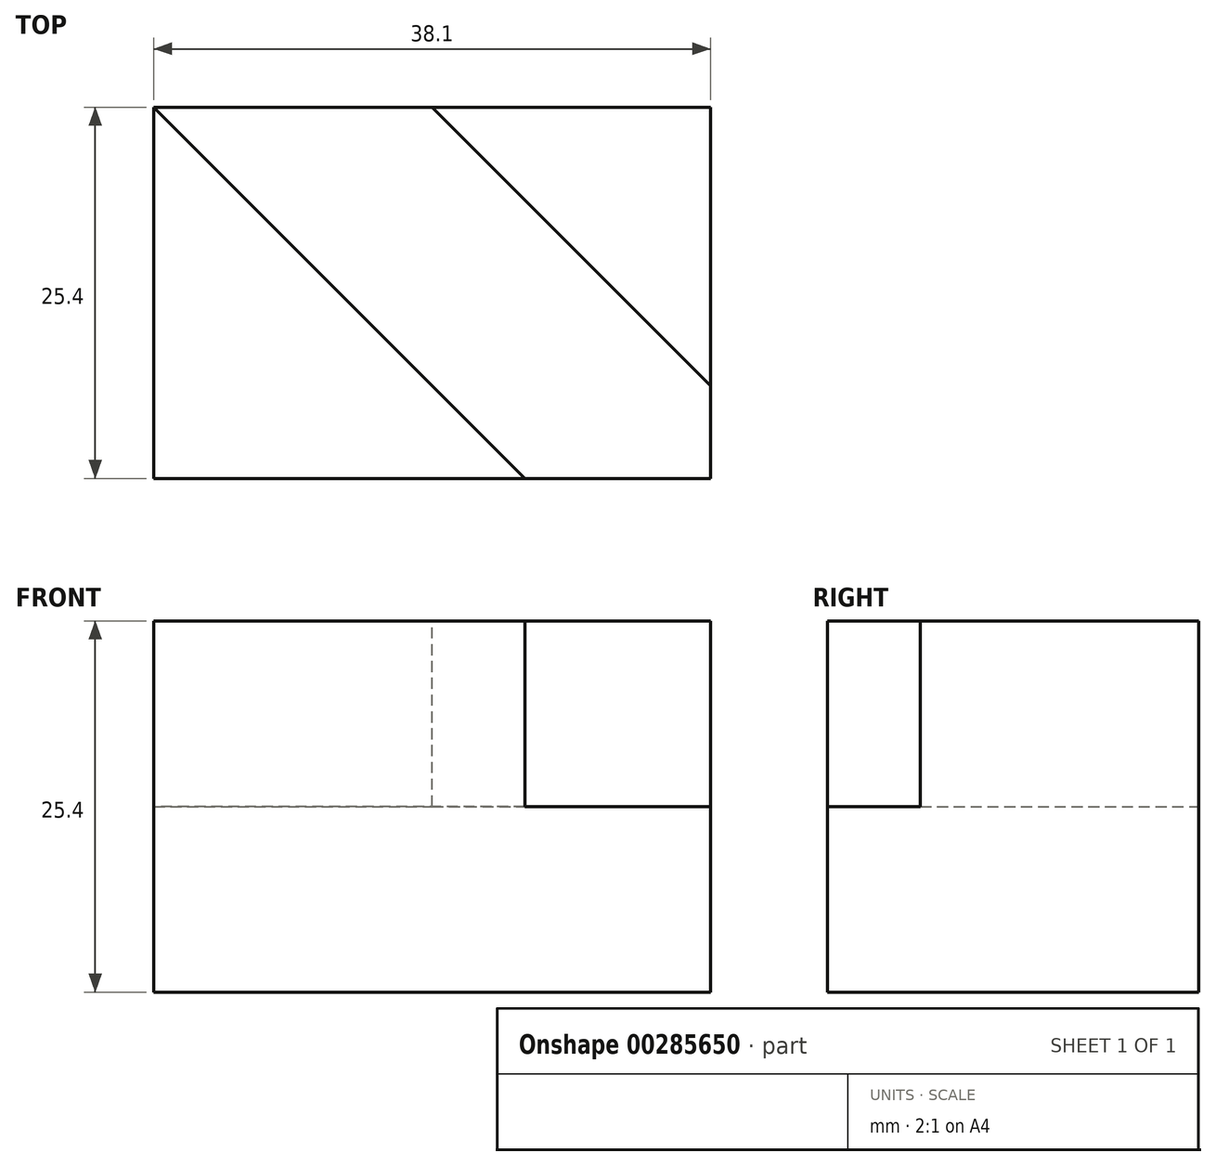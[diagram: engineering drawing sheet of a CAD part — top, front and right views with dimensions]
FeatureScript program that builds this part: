
annotation { "Feature Type Name" : "Feature", "Feature Type Description" : "" }
export const myFeature = defineFeature(function(context is Context, id is Id, definition is map)
    precondition{}
    {
        {
            var Q0;
            Q0=qCreatedBy(makeId("Front.planeOp"),FACE);
            var sketch = newSketch(context, id + "F0", { "sketchPlane" : qUnion([Q0])});
            skLineSegment(sketch, "E0", {"start": v(0, 0) * mm, "end": v(0, 25.4) * mm});
            skLineSegment(sketch, "E1", {"start": v(0, 25.4) * mm, "end": v(38.1, 25.4) * mm});
            skLineSegment(sketch, "E2", {"start": v(38.1, 25.4) * mm, "end": v(38.1, 0) * mm});
            skLineSegment(sketch, "E3", {"start": v(38.1, 0) * mm, "end": v(0, 0) * mm});
            skSolve(sketch);
        }
        {
            var Q0;
            Q0 = qSketchRegion(id + "F0", true);
            extrude(context, id + "F1", {"entities" : qUnion([Q0]), "depth" : 25.4 * mm});
        }
        {
            var Q0;
            Q0=makeQuery(id+"F1.opExtrude","CAP_FACE",FACE,{"disambiguationData":[OSD([sQuery(id+"F0.wireOp",EDGE,"E0"),sQuery(id+"F0.wireOp",EDGE,"E1"),sQuery(id+"F0.wireOp",EDGE,"E2"),sQuery(id+"F0.wireOp",EDGE,"E3")])],"isStart":false});
            var sketch = newSketch(context, id + "F2", { "sketchPlane" : qUnion([Q0])});
            skLineSegment(sketch, "E4", {"start": v(25.4, 25.4) * mm, "end": v(25.4, 12.7) * mm});
            skLineSegment(sketch, "E5", {"start": v(25.4, 12.7) * mm, "end": v(38.1, 12.7) * mm});
            skLineSegment(sketch, "E6", {"start": v(38.1, 12.7) * mm, "end": v(38.1, 25.4) * mm});
            skLineSegment(sketch, "E7", {"start": v(38.1, 25.4) * mm, "end": v(25.4, 25.4) * mm});
            skSolve(sketch);
        }
        {
            var Q0;
            Q0 = qSketchRegion(id + "F2", true);
            extrude(context, id + "F3", {"entities" : qUnion([Q0]), "operationType" : NewBodyOperationType.REMOVE, "oppositeDirection" : true, "depth" : 6.35 * mm});
        }
        {
            var Q0;
            Q0=makeQuery(id+"F1.opExtrude","SWEPT_FACE",FACE,{"disambiguationData":[OSD([sQuery(id+"F0.wireOp",EDGE,"E1")])]});
            var sketch = newSketch(context, id + "F4", { "sketchPlane" : qUnion([Q0])});
            skLineSegment(sketch, "E8", {"start": v(25.4, -25.4) * mm, "end": v(0, 0) * mm});
            skLineSegment(sketch, "E9", {"start": v(0, 0) * mm, "end": v(19.05, 0) * mm});
            skLineSegment(sketch, "E10", {"start": v(19.05, 0) * mm, "end": v(38.1, -19.05) * mm});
            skLineSegment(sketch, "E11", {"start": v(38.1, -19.05) * mm, "end": v(25.4, -19.05) * mm});
            skLineSegment(sketch, "E12", {"start": v(25.4, -19.05) * mm, "end": v(25.4, -25.4) * mm});
            skSolve(sketch);
        }
        {
            var Q0;
            Q0=makeQuery(id+"F4.imprint","IMPRINT",FACE,{"disambiguationData":[TD([[makeQuery(id+"F4.imprint","IMPRINT",EDGE,{"derivedFrom":sQuery(id+"F4.wireOp",EDGE,"E8")}),-1.0]])]});
            extrude(context, id + "F5", {"entities" : qUnion([Q0]), "operationType" : NewBodyOperationType.REMOVE, "oppositeDirection" : true, "depth" : 12.7 * mm});
        }
    });
